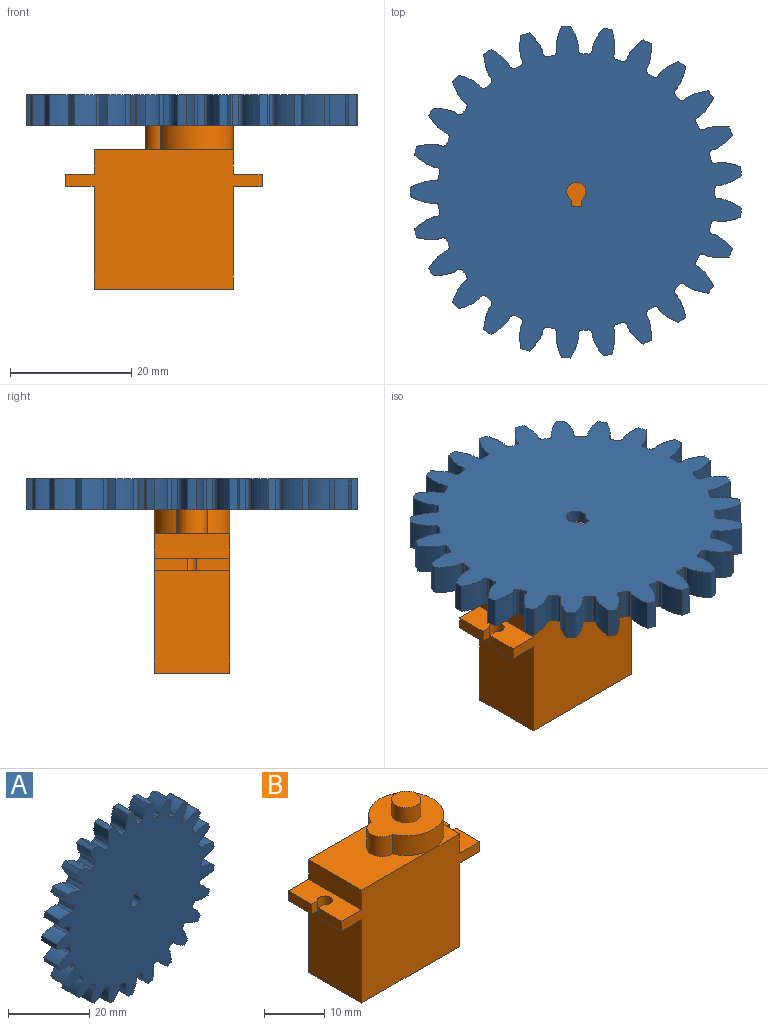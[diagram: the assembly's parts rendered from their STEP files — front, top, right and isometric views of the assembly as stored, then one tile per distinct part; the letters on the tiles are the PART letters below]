
ASSEMBLY  parts=2 mates=1
PART A: 156 faces, bbox 54.7x5.1x54.8 mm
  f0: cylinder r=27.43mm len=5.08mm, axis (0,1,0), area 7.4mm2, adj f24,f30,f141,f153
  f1: cylinder r=27.43mm len=5.08mm, axis (0,1,0), area 7.4mm2, adj f24,f30,f148,f151
  f2: cylinder r=27.43mm len=5.08mm, axis (0,1,0), area 7.4mm2, adj f24,f30,f136,f143
  f3: cylinder r=27.43mm len=5.08mm, axis (0,1,0), area 7.4mm2, adj f24,f30,f131,f138
  f4: cylinder r=27.43mm len=5.08mm, axis (0,1,0), area 7.4mm2, adj f24,f30,f126,f133
  f5: cylinder r=27.43mm len=5.08mm, axis (0,1,0), area 7.4mm2, adj f24,f30,f116,f128
  f6: cylinder r=27.43mm len=5.08mm, axis (0,1,0), area 7.4mm2, adj f24,f30,f111,f123
  f7: cylinder r=27.43mm len=5.08mm, axis (0,1,0), area 7.4mm2, adj f24,f30,f118,f121
  f8: cylinder r=27.43mm len=5.08mm, axis (0,1,0), area 7.4mm2, adj f24,f30,f106,f113
  f9: cylinder r=27.43mm len=5.08mm, axis (0,1,0), area 7.4mm2, adj f24,f30,f101,f108
  f10: cylinder r=27.43mm len=5.08mm, axis (0,1,0), area 7.4mm2, adj f24,f30,f96,f103
  f11: cylinder r=27.43mm len=5.08mm, axis (0,1,0), area 7.4mm2, adj f24,f30,f81,f98
  f12: cylinder r=27.43mm len=5.08mm, axis (0,1,0), area 7.4mm2, adj f24,f30,f31,f93
  f13: cylinder r=27.43mm len=5.08mm, axis (0,1,0), area 7.4mm2, adj f24,f30,f88,f91
  f14: cylinder r=27.43mm len=5.08mm, axis (0,1,0), area 7.4mm2, adj f24,f30,f76,f83
  f15: cylinder r=27.43mm len=5.08mm, axis (0,1,0), area 7.4mm2, adj f24,f30,f78,f86
  f16: cylinder r=27.43mm len=5.08mm, axis (0,1,0), area 7.4mm2, adj f24,f30,f73,f146
  f17: cylinder r=27.43mm len=5.08mm, axis (0,1,0), area 7.4mm2, adj f24,f30,f68,f71
  f18: cylinder r=27.43mm len=5.08mm, axis (0,1,0), area 7.4mm2, adj f24,f30,f63,f66
  f19: cylinder r=27.43mm len=5.08mm, axis (0,1,0), area 7.4mm2, adj f24,f30,f58,f61
  f20: cylinder r=27.43mm len=5.08mm, axis (0,1,0), area 7.4mm2, adj f24,f30,f46,f53
  f21: cylinder r=27.43mm len=5.08mm, axis (0,1,0), area 7.4mm2, adj f24,f30,f36,f48
  f22: cylinder r=27.43mm len=5.08mm, axis (0,1,0), area 7.4mm2, adj f24,f30,f43,f56
  f23: cylinder r=27.43mm len=5.08mm, axis (0,1,0), area 7.4mm2, adj f24,f30,f38,f41
  f24: plane 54.85x54.74mm, normal (0,-1,0), area 1985mm2, adj f0,f1,f2,f3,f4,f5,f6,f7
  f25: plane 5.08x1.01mm, normal (-1,0,0), area 5.1mm2, adj f24,f26,f28,f30
  f26: cylinder r=1.59mm len=5.08mm, axis (0,1,0), area 42.2mm2, adj f24,f25,f27,f30
  f27: plane 5.08x1.01mm, normal (1,0,0), area 5.1mm2, adj f24,f26,f28,f30
  f28: plane 5.08x1.59mm, normal (0,0,-1), area 8.1mm2, adj f24,f25,f27,f30
  f29: cylinder r=27.43mm len=5.08mm, axis (0,1,0), area 7.4mm2, adj f24,f30,f33,f51
  f30: plane 54.85x54.74mm, normal (0,1,0), area 1985mm2, adj f0,f1,f2,f3,f4,f5,f6,f7
  f31: extruded ~5.08x3.89mm, area 21.7mm2, adj f12,f24,f30,f34
  f32: cylinder r=22.86mm len=5.08mm, axis (0,1,0), area 5.4mm2, adj f24,f30,f34,f35
  f33: extruded ~5.08x3.89mm, area 21.7mm2, adj f24,f29,f30,f35
  f34: cylinder r=0.58mm len=5.08mm, axis (0,1,0), area 4.5mm2, adj f24,f30,f31,f32
  f35: cylinder r=0.58mm len=5.08mm, axis (0,1,0), area 4.5mm2, adj f24,f30,f32,f33
  f36: extruded ~5.08x3.93mm, area 21.7mm2, adj f21,f24,f30,f39
  f37: cylinder r=22.86mm len=5.08mm, axis (0,1,0), area 5.4mm2, adj f24,f30,f39,f40
  f38: extruded ~5.08x3.83mm, area 21.7mm2, adj f23,f24,f30,f40
  f39: cylinder r=0.58mm len=5.08mm, axis (0,1,0), area 4.5mm2, adj f24,f30,f36,f37
  f40: cylinder r=0.58mm len=5.08mm, axis (0,1,0), area 4.5mm2, adj f24,f30,f37,f38
  f41: extruded ~5.08x3.43mm, area 21.7mm2, adj f23,f24,f30,f44
  f42: cylinder r=22.86mm len=5.08mm, axis (0,1,0), area 5.4mm2, adj f24,f30,f44,f45
  f43: extruded ~5.08x4.14mm, area 21.7mm2, adj f22,f24,f30,f45
  f44: cylinder r=0.58mm len=5.08mm, axis (0,1,0), area 4.5mm2, adj f24,f30,f41,f42
  f45: cylinder r=0.58mm len=5.08mm, axis (0,1,0), area 4.5mm2, adj f24,f30,f42,f43
  f46: extruded ~5.08x4.18mm, area 21.7mm2, adj f20,f24,f30,f49
  f47: cylinder r=22.86mm len=5.08mm, axis (0,1,0), area 5.4mm2, adj f24,f30,f49,f50
  f48: extruded ~5.08x3.27mm, area 21.7mm2, adj f21,f24,f30,f50
  f49: cylinder r=0.58mm len=5.08mm, axis (0,1,0), area 4.5mm2, adj f24,f30,f46,f47
  f50: cylinder r=0.58mm len=5.08mm, axis (0,1,0), area 4.5mm2, adj f24,f30,f47,f48
  f51: extruded ~5.08x4.17mm, area 21.7mm2, adj f24,f29,f30,f54
  f52: cylinder r=22.86mm len=5.08mm, axis (0,1,0), area 5.4mm2, adj f24,f30,f54,f55
  f53: extruded ~5.08x3.38mm, area 21.7mm2, adj f20,f24,f30,f55
  f54: cylinder r=0.58mm len=5.08mm, axis (0,1,0), area 4.5mm2, adj f24,f30,f51,f52
  f55: cylinder r=0.58mm len=5.08mm, axis (0,1,0), area 4.5mm2, adj f24,f30,f52,f53
  f56: extruded ~5.08x3.21mm, area 21.7mm2, adj f22,f24,f30,f59
  f57: cylinder r=22.86mm len=5.08mm, axis (0,1,0), area 5.4mm2, adj f24,f30,f59,f60
  f58: extruded ~5.08x4.2mm, area 21.7mm2, adj f19,f24,f30,f60
  f59: cylinder r=0.58mm len=5.08mm, axis (0,1,0), area 4.5mm2, adj f24,f30,f56,f57
  f60: cylinder r=0.58mm len=5.08mm, axis (0,1,0), area 4.5mm2, adj f24,f30,f57,f58
  f61: extruded ~5.08x3.79mm, area 21.7mm2, adj f19,f24,f30,f64
  f62: cylinder r=22.86mm len=5.08mm, axis (0,1,0), area 5.4mm2, adj f24,f30,f64,f65
  f63: extruded ~5.08x3.99mm, area 21.7mm2, adj f18,f24,f30,f65
  f64: cylinder r=0.58mm len=5.08mm, axis (0,1,0), area 4.5mm2, adj f24,f30,f61,f62
  f65: cylinder r=0.58mm len=5.08mm, axis (0,1,0), area 4.5mm2, adj f24,f30,f62,f63
  f66: extruded ~5.08x4.12mm, area 21.7mm2, adj f18,f24,f30,f69
  f67: cylinder r=22.86mm len=5.08mm, axis (0,1,0), area 5.4mm2, adj f24,f30,f69,f70
  f68: extruded ~5.08x3.53mm, area 21.7mm2, adj f17,f24,f30,f70
  f69: cylinder r=0.58mm len=5.08mm, axis (0,1,0), area 4.5mm2, adj f24,f30,f66,f67
  f70: cylinder r=0.58mm len=5.08mm, axis (0,1,0), area 4.5mm2, adj f24,f30,f67,f68
  f71: extruded ~5.08x4.2mm, area 21.7mm2, adj f17,f24,f30,f74
  f72: cylinder r=22.86mm len=5.08mm, axis (0,1,0), area 5.4mm2, adj f24,f30,f74,f75
  f73: extruded ~5.08x3.1mm, area 21.7mm2, adj f16,f24,f30,f75
  f74: cylinder r=0.58mm len=5.08mm, axis (0,1,0), area 4.5mm2, adj f24,f30,f71,f72
  f75: cylinder r=0.58mm len=5.08mm, axis (0,1,0), area 4.5mm2, adj f24,f30,f72,f73
  f76: extruded ~5.08x3.83mm, area 21.7mm2, adj f14,f24,f30,f79
  f77: cylinder r=22.86mm len=5.08mm, axis (0,1,0), area 5.4mm2, adj f24,f30,f79,f80
  f78: extruded ~5.08x3.93mm, area 21.7mm2, adj f15,f24,f30,f80
  f79: cylinder r=0.58mm len=5.08mm, axis (0,1,0), area 4.5mm2, adj f24,f30,f76,f77
  f80: cylinder r=0.58mm len=5.08mm, axis (0,1,0), area 4.5mm2, adj f24,f30,f77,f78
  f81: extruded ~5.08x4.14mm, area 21.7mm2, adj f11,f24,f30,f84
  f82: cylinder r=22.86mm len=5.08mm, axis (0,1,0), area 5.4mm2, adj f24,f30,f84,f85
  f83: extruded ~5.08x3.43mm, area 21.7mm2, adj f14,f24,f30,f85
  f84: cylinder r=0.58mm len=5.08mm, axis (0,1,0), area 4.5mm2, adj f24,f30,f81,f82
  f85: cylinder r=0.58mm len=5.08mm, axis (0,1,0), area 4.5mm2, adj f24,f30,f82,f83
  f86: extruded ~5.08x3.27mm, area 21.7mm2, adj f15,f24,f30,f89
  f87: cylinder r=22.86mm len=5.08mm, axis (0,1,0), area 5.4mm2, adj f24,f30,f89,f90
  f88: extruded ~5.08x4.18mm, area 21.7mm2, adj f13,f24,f30,f90
  f89: cylinder r=0.58mm len=5.08mm, axis (0,1,0), area 4.5mm2, adj f24,f30,f86,f87
  f90: cylinder r=0.58mm len=5.08mm, axis (0,1,0), area 4.5mm2, adj f24,f30,f87,f88
  f91: extruded ~5.08x3.38mm, area 21.7mm2, adj f13,f24,f30,f94
  f92: cylinder r=22.86mm len=5.08mm, axis (0,1,0), area 5.4mm2, adj f24,f30,f94,f95
  f93: extruded ~5.08x4.17mm, area 21.7mm2, adj f12,f24,f30,f95
  f94: cylinder r=0.58mm len=5.08mm, axis (0,1,0), area 4.5mm2, adj f24,f30,f91,f92
  f95: cylinder r=0.58mm len=5.08mm, axis (0,1,0), area 4.5mm2, adj f24,f30,f92,f93
  f96: extruded ~5.08x4.2mm, area 21.7mm2, adj f10,f24,f30,f99
  f97: cylinder r=22.86mm len=5.08mm, axis (0,1,0), area 5.4mm2, adj f24,f30,f99,f100
  f98: extruded ~5.08x3.21mm, area 21.7mm2, adj f11,f24,f30,f100
  f99: cylinder r=0.58mm len=5.08mm, axis (0,1,0), area 4.5mm2, adj f24,f30,f96,f97
  f100: cylinder r=0.58mm len=5.08mm, axis (0,1,0), area 4.5mm2, adj f24,f30,f97,f98
  f101: extruded ~5.08x3.99mm, area 21.7mm2, adj f9,f24,f30,f104
  f102: cylinder r=22.86mm len=5.08mm, axis (0,1,0), area 5.4mm2, adj f24,f30,f104,f105
  f103: extruded ~5.08x3.79mm, area 21.7mm2, adj f10,f24,f30,f105
  f104: cylinder r=0.58mm len=5.08mm, axis (0,1,0), area 4.5mm2, adj f24,f30,f101,f102
  f105: cylinder r=0.58mm len=5.08mm, axis (0,1,0), area 4.5mm2, adj f24,f30,f102,f103
  f106: extruded ~5.08x3.53mm, area 21.7mm2, adj f8,f24,f30,f109
  f107: cylinder r=22.86mm len=5.08mm, axis (0,1,0), area 5.4mm2, adj f24,f30,f109,f110
  f108: extruded ~5.08x4.12mm, area 21.7mm2, adj f9,f24,f30,f110
  f109: cylinder r=0.58mm len=5.08mm, axis (0,1,0), area 4.5mm2, adj f24,f30,f106,f107
  f110: cylinder r=0.58mm len=5.08mm, axis (0,1,0), area 4.5mm2, adj f24,f30,f107,f108
  f111: extruded ~5.08x3.1mm, area 21.7mm2, adj f6,f24,f30,f114
  f112: cylinder r=22.86mm len=5.08mm, axis (0,1,0), area 5.4mm2, adj f24,f30,f114,f115
  f113: extruded ~5.08x4.2mm, area 21.7mm2, adj f8,f24,f30,f115
  f114: cylinder r=0.58mm len=5.08mm, axis (0,1,0), area 4.5mm2, adj f24,f30,f111,f112
  f115: cylinder r=0.58mm len=5.08mm, axis (0,1,0), area 4.5mm2, adj f24,f30,f112,f113
  f116: extruded ~5.08x4.09mm, area 21.7mm2, adj f5,f24,f30,f119
  f117: cylinder r=22.86mm len=5.08mm, axis (0,1,0), area 5.4mm2, adj f24,f30,f119,f120
  f118: extruded ~5.08x3.58mm, area 21.7mm2, adj f7,f24,f30,f120
  f119: cylinder r=0.58mm len=5.08mm, axis (0,1,0), area 4.5mm2, adj f24,f30,f116,f117
  f120: cylinder r=0.58mm len=5.08mm, axis (0,1,0), area 4.5mm2, adj f24,f30,f117,f118
  f121: extruded ~5.08x3.71mm, area 21.7mm2, adj f7,f24,f30,f124
  f122: cylinder r=22.86mm len=5.08mm, axis (0,1,0), area 5.4mm2, adj f24,f30,f124,f125
  f123: extruded ~5.08x4.02mm, area 21.7mm2, adj f6,f24,f30,f125
  f124: cylinder r=0.58mm len=5.08mm, axis (0,1,0), area 4.5mm2, adj f24,f30,f121,f122
  f125: cylinder r=0.58mm len=5.08mm, axis (0,1,0), area 4.5mm2, adj f24,f30,f122,f123
  f126: extruded ~5.08x4.21mm, area 21.7mm2, adj f4,f24,f30,f129
  f127: cylinder r=22.86mm len=5.08mm, axis (0,1,0), area 5.4mm2, adj f24,f30,f129,f130
  f128: extruded ~5.08x3.03mm, area 21.7mm2, adj f5,f24,f30,f130
  f129: cylinder r=0.58mm len=5.08mm, axis (0,1,0), area 4.5mm2, adj f24,f30,f126,f127
  f130: cylinder r=0.58mm len=5.08mm, axis (0,1,0), area 4.5mm2, adj f24,f30,f127,f128
  f131: extruded ~5.08x4.06mm, area 21.7mm2, adj f3,f24,f30,f134
  f132: cylinder r=22.86mm len=5.08mm, axis (0,1,0), area 5.4mm2, adj f24,f30,f134,f135
  f133: extruded ~5.08x3.66mm, area 21.7mm2, adj f4,f24,f30,f135
  f134: cylinder r=0.58mm len=5.08mm, axis (0,1,0), area 4.5mm2, adj f24,f30,f131,f132
  f135: cylinder r=0.58mm len=5.08mm, axis (0,1,0), area 4.5mm2, adj f24,f30,f132,f133
  f136: extruded ~5.08x3.66mm, area 21.7mm2, adj f2,f24,f30,f139
  f137: cylinder r=22.86mm len=5.08mm, axis (0,1,0), area 5.4mm2, adj f24,f30,f139,f140
  f138: extruded ~5.08x4.06mm, area 21.7mm2, adj f3,f24,f30,f140
  f139: cylinder r=0.58mm len=5.08mm, axis (0,1,0), area 4.5mm2, adj f24,f30,f136,f137
  f140: cylinder r=0.58mm len=5.08mm, axis (0,1,0), area 4.5mm2, adj f24,f30,f137,f138
  f141: extruded ~5.08x3.03mm, area 21.7mm2, adj f0,f24,f30,f144
  f142: cylinder r=22.86mm len=5.08mm, axis (0,1,0), area 5.4mm2, adj f24,f30,f144,f145
  f143: extruded ~5.08x4.21mm, area 21.7mm2, adj f2,f24,f30,f145
  f144: cylinder r=0.58mm len=5.08mm, axis (0,1,0), area 4.5mm2, adj f24,f30,f141,f142
  f145: cylinder r=0.58mm len=5.08mm, axis (0,1,0), area 4.5mm2, adj f24,f30,f142,f143
  f146: extruded ~5.08x4.02mm, area 21.7mm2, adj f16,f24,f30,f149
  f147: cylinder r=22.86mm len=5.08mm, axis (0,1,0), area 5.4mm2, adj f24,f30,f149,f150
  f148: extruded ~5.08x3.71mm, area 21.7mm2, adj f1,f24,f30,f150
  f149: cylinder r=0.58mm len=5.08mm, axis (0,1,0), area 4.5mm2, adj f24,f30,f146,f147
  f150: cylinder r=0.58mm len=5.08mm, axis (0,1,0), area 4.5mm2, adj f24,f30,f147,f148
  f151: extruded ~5.08x3.58mm, area 21.7mm2, adj f1,f24,f30,f154
  f152: cylinder r=22.86mm len=5.08mm, axis (0,1,0), area 5.4mm2, adj f24,f30,f154,f155
  f153: extruded ~5.08x4.09mm, area 21.7mm2, adj f0,f24,f30,f155
  f154: cylinder r=0.58mm len=5.08mm, axis (0,1,0), area 4.5mm2, adj f24,f30,f151,f152
  f155: cylinder r=0.58mm len=5.08mm, axis (0,1,0), area 4.5mm2, adj f24,f30,f152,f153
PART B: 29 faces, bbox 32.5x12.6x30 mm
  f0: plane 4.99x4.9mm, normal (0,0,1), area 18.9mm2, adj f1
  f1: cylinder r=2.45mm len=4.9mm, axis (0,0,1), area 46.2mm2, adj f0,f2
  f2: plane 14.61x12.65mm, normal (0,0,1), area 112mm2, adj f1,f3,f4
  f3: cylinder r=2.5mm len=5mm, axis (0,0,1), area 31.6mm2, adj f2,f4,f10
  f4: cylinder r=6.25mm len=12.5mm, axis (0,0,1), area 136.5mm2, adj f2,f3,f8,f10,f11
  f5: plane 2x1.38mm, normal (0,-1,0), area 2.7mm2, adj f6,f9,f13,f15
  f6: cylinder r=1.25mm len=2.5mm, axis (0,0,-1), area 12.5mm2, adj f5,f7,f13,f15
  f7: plane 2x1.38mm, normal (0,1,0), area 2.7mm2, adj f6,f13,f14,f15
  f8: plane 6.25x6.25mm, normal (0,0,1), area 8.4mm2, adj f4,f12,f20
  f9: plane 5.5x2mm, normal (1,0,0), area 11mm2, adj f5,f13,f15,f20
  f10: plane 16.75x12.5mm, normal (0,0,1), area 139.8mm2, adj f3,f4,f18,f20,f22
  f11: plane 6.25x6.25mm, normal (0,0,1), area 8.4mm2, adj f4,f12,f22
  f12: plane 12.5x4mm, normal (1,0,0), area 50mm2, adj f8,f11,f13,f20,f22
  f13: plane 12.5x4.75mm, normal (0,0,1), area 52.7mm2, adj f5,f6,f7,f9,f12,f14,f20,f22
  f14: plane 5.5x2mm, normal (1,0,0), area 11mm2, adj f7,f13,f15,f22
  f15: plane 12.5x4.75mm, normal (0,0,-1), area 52.7mm2, adj f5,f6,f7,f9,f14,f16,f20,f22
  f16: plane 17x12.5mm, normal (1,0,0), area 212.5mm2, adj f15,f17,f20,f22
  f17: plane 23x12.5mm, normal (0,0,-1), area 287.5mm2, adj f16,f20,f21,f22
  f18: plane 12.5x4mm, normal (-1,0,0), area 50mm2, adj f10,f20,f22,f25
  f19: plane 5.5x2mm, normal (-1,0,0), area 11mm2, adj f20,f24,f25,f27
  f20: plane 32.5x23mm, normal (0,1,0), area 548mm2, adj f8,f9,f10,f12,f13,f15,f16,f17
  f21: plane 17x12.5mm, normal (-1,0,0), area 212.5mm2, adj f17,f20,f22,f27
  f22: plane 32.5x23mm, normal (0,-1,0), area 548mm2, adj f10,f11,f12,f13,f14,f15,f16,f17
  f23: plane 5.5x2mm, normal (-1,0,0), area 11mm2, adj f22,f25,f26,f27
  f24: plane 2x1.38mm, normal (0,-1,0), area 2.8mm2, adj f19,f25,f27,f28
  f25: plane 12.5x4.75mm, normal (0,0,1), area 52.7mm2, adj f18,f19,f20,f22,f23,f24,f26,f28
  f26: plane 2x1.38mm, normal (0,1,0), area 2.8mm2, adj f23,f25,f27,f28
  f27: plane 12.5x4.75mm, normal (0,0,-1), area 52.7mm2, adj f19,f20,f21,f22,f23,f24,f26,f28
  f28: cylinder r=1.25mm len=2.5mm, axis (0,0,-1), area 12.5mm2, adj f24,f25,f26,f27
PLACE A rot(axis=(1,0,0),90deg) t=(-4.18,9.36,39.58)mm
PLACE B t=(2.58,3.11,7.5)mm
MATE fastened A.f0 <-> B.f2  axis (0,0,-1) through (-4.18,9.36,34.5)mm
